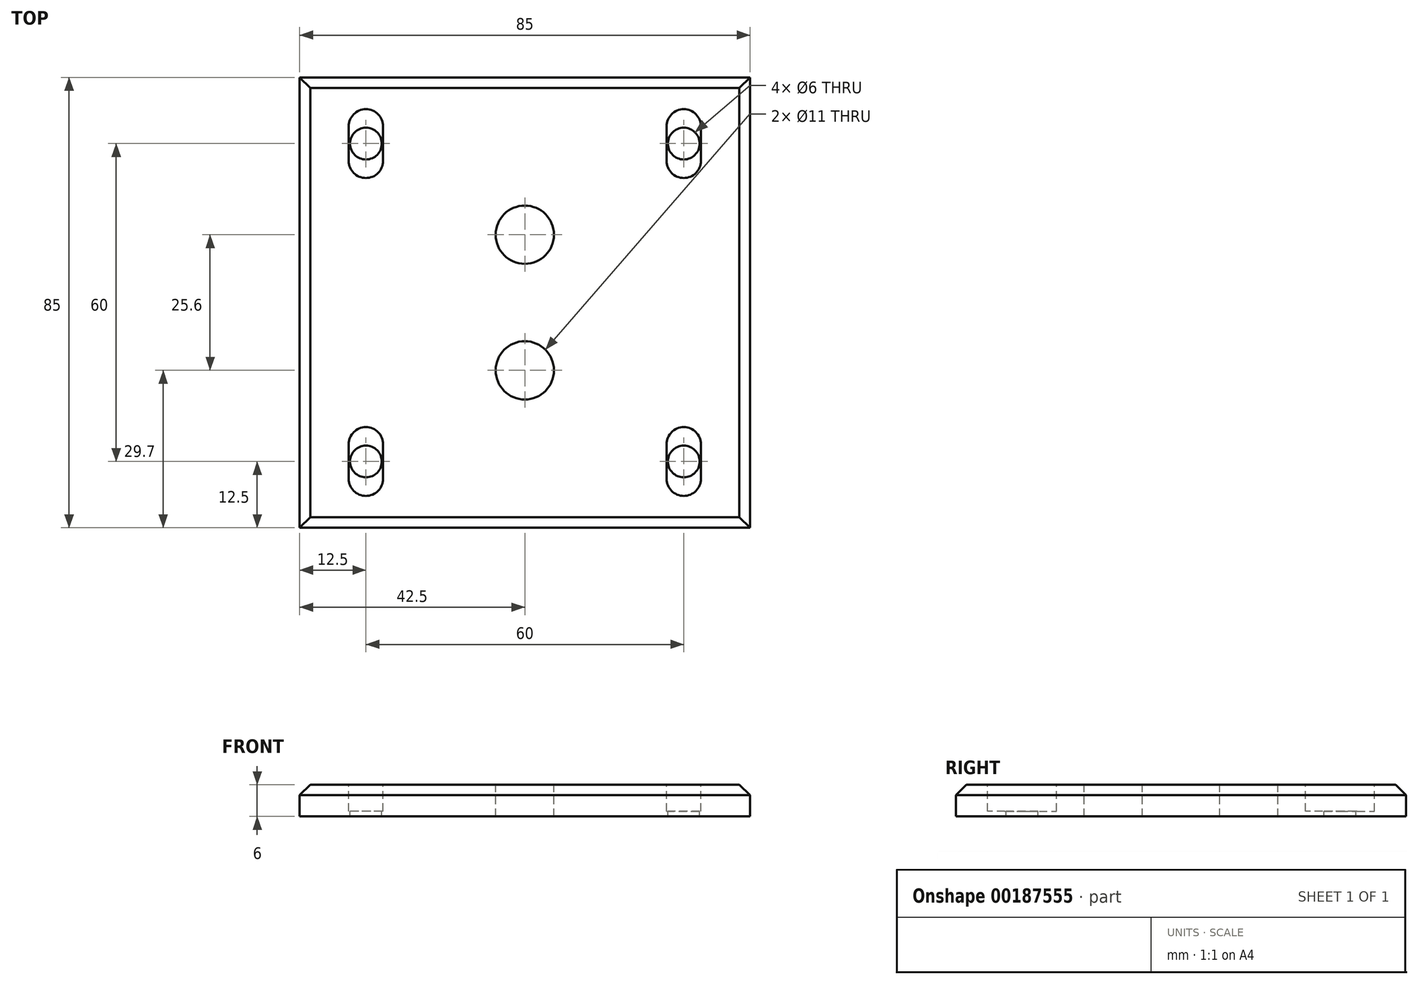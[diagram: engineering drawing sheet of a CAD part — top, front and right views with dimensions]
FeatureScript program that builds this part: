
annotation { "Feature Type Name" : "Feature", "Feature Type Description" : "" }
export const myFeature = defineFeature(function(context is Context, id is Id, definition is map)
    precondition{}
    {
        {
            var Q0;
            Q0=qCreatedBy(makeId("Top.planeOp"),FACE);
            var sketch = newSketch(context, id + "F0", { "sketchPlane" : qUnion([Q0])});
            skLineSegment(sketch, "E0.bottom", {"start": v(42.5, 42.5) * mm, "end": v(-42.5, 42.5) * mm});
            skLineSegment(sketch, "E0.top", {"start": v(42.5, -42.5) * mm, "end": v(-42.5, -42.5) * mm});
            skLineSegment(sketch, "E0.left", {"start": v(42.5, 42.5) * mm, "end": v(42.5, -42.5) * mm});
            skLineSegment(sketch, "E0.right", {"start": v(-42.5, 42.5) * mm, "end": v(-42.5, -42.5) * mm});
            skPoint(sketch, "E0.middle", {"position": v(0, 0) * mm});
            skSolve(sketch);
        }
        {
            var Q0;
            Q0=makeQuery(id+"F0.imprint","IMPRINT",FACE,{"disambiguationData":[TD([[makeQuery(id+"F0.imprint","IMPRINT",EDGE,{"derivedFrom":sQuery(id+"F0.wireOp",EDGE,"E0.bottom")}),1.0]])]});
            extrude(context, id + "F1", {"entities" : qUnion([Q0]), "depth" : 6 * mm});
        }
        {
            var Q0;
            Q0=makeQuery(id+"F1.opExtrude","CAP_FACE",FACE,{"disambiguationData":[OSD([sQuery(id+"F0.wireOp",EDGE,"E0.bottom"),sQuery(id+"F0.wireOp",EDGE,"E0.top"),sQuery(id+"F0.wireOp",EDGE,"E0.left"),sQuery(id+"F0.wireOp",EDGE,"E0.right")])],"isStart":false});
            var sketch = newSketch(context, id + "F2", { "sketchPlane" : qUnion([Q0])});
            skLineSegment(sketch, "E1", {"start": v(0, 42.5) * mm, "end": v(0, -42.5) * mm, "construction": true});
            skCircle(sketch, "E2", {"center": v(0, 12.8) * mm, "radius": 5.5 * mm});
            skCircle(sketch, "E3.MirrorC", {"center": v(0, -12.8) * mm, "radius": 5.5 * mm});
            skSolve(sketch);
        }
        {
            var Q0;
            Q0=qSketchRegion(id+"F2",true);
            extrude(context, id + "F3", {"entities" : qUnion([Q0]), "operationType" : NewBodyOperationType.REMOVE, "endBound" : BoundingType.THROUGH_ALL, "oppositeDirection" : true, "depth" : 25 * mm});
        }
        {
            var Q0;
            Q0=makeQuery(id+"F1.opExtrude","CAP_FACE",FACE,{"disambiguationData":[OSD([sQuery(id+"F0.wireOp",EDGE,"E0.bottom"),sQuery(id+"F0.wireOp",EDGE,"E0.top"),sQuery(id+"F0.wireOp",EDGE,"E0.left"),sQuery(id+"F0.wireOp",EDGE,"E0.right")])],"isStart":false});
            var sketch = newSketch(context, id + "F4", { "sketchPlane" : qUnion([Q0])});
            skLineSegment(sketch, "E4", {"start": v(-42.5, 0) * mm, "end": v(42.5, 0) * mm, "construction": true});
            skLineSegment(sketch, "E5.bottom", {"start": v(30, 30) * mm, "end": v(-30, 30) * mm, "construction": true});
            skLineSegment(sketch, "E5.top", {"start": v(30, -30) * mm, "end": v(-30, -30) * mm, "construction": true});
            skLineSegment(sketch, "E5.left", {"start": v(30, 30) * mm, "end": v(30, -30) * mm, "construction": true});
            skLineSegment(sketch, "E5.right", {"start": v(-30, 30) * mm, "end": v(-30, -30) * mm, "construction": true});
            skPoint(sketch, "E5.middle", {"position": v(0, 0) * mm});
            skCircle(sketch, "E6", {"center": v(-30, 30) * mm, "radius": 8.25 * mm, "construction": true});
            skCircle(sketch, "E7", {"center": v(30, 30) * mm, "radius": 8.25 * mm, "construction": true});
            skCircle(sketch, "E8", {"center": v(30, -30) * mm, "radius": 8.25 * mm, "construction": true});
            skCircle(sketch, "E9", {"center": v(-30, -30) * mm, "radius": 8.25 * mm, "construction": true});
            skCircle(sketch, "E10", {"center": v(30, 30) * mm, "radius": 8 * mm});
            skCircle(sketch, "E11", {"center": v(30, -30) * mm, "radius": 8 * mm});
            skCircle(sketch, "E12", {"center": v(-30, -30) * mm, "radius": 8 * mm});
            skCircle(sketch, "E13", {"center": v(-30, 30) * mm, "radius": 8 * mm});
            skSolve(sketch);
        }
        {
            var Q0;
            Q0=sQuery(id+"F4.wireOp",VERTEX,"E5.right.end");
            var Q1;
            Q1=sQuery(id+"F4.wireOp",VERTEX,"E13.center");
            var Q2;
            Q2=sQuery(id+"F4.wireOp",VERTEX,"E7.center");
            var Q3;
            Q3=sQuery(id+"F4.wireOp",VERTEX,"E5.left.end");
            var Q4;
            Q4=makeQuery(id+"F1.opExtrude","SWEPT_BODY",BODY,{"disambiguationData":[OSD([sQuery(id+"F0.wireOp",EDGE,"E0.bottom"),sQuery(id+"F0.wireOp",EDGE,"E0.top"),sQuery(id+"F0.wireOp",EDGE,"E0.left"),sQuery(id+"F0.wireOp",EDGE,"E0.right")])]});
            hole(context, id + "F5", {"style" : HoleStyle.SIMPLE, "endStyle" : HoleEndStyle.THROUGH, "holeDiameter" : 6 * mm, "locations" : qUnion([Q0, Q1, Q2, Q3]), "scope" : qUnion([Q4]), "isTappedThrough" : true});
        }
        {
            var Q0;
            Q0=makeQuery(id+"F1.opExtrude","CAP_EDGE",EDGE,{"disambiguationData":[OSD([sQuery(id+"F0.wireOp",EDGE,"E0.right")])],"isStart":false});
            var Q1;
            Q1=makeQuery(id+"F1.opExtrude","CAP_EDGE",EDGE,{"disambiguationData":[OSD([sQuery(id+"F0.wireOp",EDGE,"E0.top")])],"isStart":false});
            var Q2;
            Q2=makeQuery(id+"F1.opExtrude","CAP_EDGE",EDGE,{"disambiguationData":[OSD([sQuery(id+"F0.wireOp",EDGE,"E0.left")])],"isStart":false});
            var Q3;
            Q3=makeQuery(id+"F1.opExtrude","CAP_EDGE",EDGE,{"disambiguationData":[OSD([sQuery(id+"F0.wireOp",EDGE,"E0.bottom")])],"isStart":false});
            chamfer(context, id + "F6", {"entities" : qUnion([Q0, Q1, Q2, Q3]), "width" : 2 * mm, "tangentPropagation" : true});
        }
        {
            var Q0;
            Q0=makeQuery(id+"F4.imprint","IMPRINT",FACE,{"disambiguationData":[TD([[makeQuery(id+"F4.imprint","IMPRINT",EDGE,{"derivedFrom":sQuery(id+"F4.wireOp",EDGE,"E10")}),-1.0]])]});
            var sketch = newSketch(context, id + "F7", { "sketchPlane" : qUnion([Q0])});
            skPoint(sketch, "E14.0", {"position": v(30, 30) * mm});
            skPoint(sketch, "E15.0", {"position": v(-30, 30) * mm});
            skPoint(sketch, "E16.0", {"position": v(30, -30) * mm});
            skPoint(sketch, "E17.0", {"position": v(-30, -30) * mm});
            skCircle(sketch, "E18", {"center": v(30, 30) * mm, "radius": 3.25 * mm, "construction": true});
            skLineSegment(sketch, "E19.0", {"start": v(30, 33.25) * mm, "end": v(30, 26.75) * mm, "construction": true});
            skLineSegment(sketch, "E20.0", {"start": v(-30, 30) * mm, "end": v(-30, -30) * mm, "construction": true});
            skLineSegment(sketch, "E21.0", {"start": v(30, -30) * mm, "end": v(-30, -30) * mm, "construction": true});
            skArc(sketch, "E22.0.startCap", {"start": v(26.75, 33.25) * mm, "mid": v(30, 36.5) * mm, "end": v(33.25, 33.25) * mm});
            skArc(sketch, "E22.0.endCap", {"start": v(33.25, 26.75) * mm, "mid": v(30, 23.5) * mm, "end": v(26.75, 26.75) * mm});
            skLineSegment(sketch, "E22.0.left", {"start": v(33.25, 33.25) * mm, "end": v(33.25, 26.75) * mm});
            skLineSegment(sketch, "E22.0.right", {"start": v(26.75, 33.25) * mm, "end": v(26.75, 26.75) * mm});
            skCircle(sketch, "E23.MirrorC", {"center": v(-30, 30) * mm, "radius": 3.25 * mm, "construction": true});
            skArc(sketch, "E24.MirrorCS", {"start": v(-26.75, 33.25) * mm, "mid": v(-30, 36.5) * mm, "end": v(-33.25, 33.25) * mm});
            skArc(sketch, "E25.MirrorCS", {"start": v(-33.25, 26.75) * mm, "mid": v(-30, 23.5) * mm, "end": v(-26.75, 26.75) * mm});
            skLineSegment(sketch, "E26.MirrorCS", {"start": v(-33.25, 33.25) * mm, "end": v(-33.25, 26.75) * mm});
            skLineSegment(sketch, "E27.MirrorCS", {"start": v(-30, 33.25) * mm, "end": v(-30, 26.75) * mm, "construction": true});
            skLineSegment(sketch, "E28.MirrorCS", {"start": v(-26.75, 33.25) * mm, "end": v(-26.75, 26.75) * mm});
            skLineSegment(sketch, "E29.MirrorCS", {"start": v(-30, -33.25) * mm, "end": v(-30, -26.75) * mm, "construction": true});
            skLineSegment(sketch, "E30.MirrorCS", {"start": v(30, -33.25) * mm, "end": v(30, -26.75) * mm, "construction": true});
            skArc(sketch, "E31.MirrorCS", {"start": v(26.75, -33.25) * mm, "mid": v(30, -36.5) * mm, "end": v(33.25, -33.25) * mm});
            skLineSegment(sketch, "E32.MirrorCS", {"start": v(-26.75, -33.25) * mm, "end": v(-26.75, -26.75) * mm});
            skArc(sketch, "E33.MirrorCS", {"start": v(-33.25, -26.75) * mm, "mid": v(-30, -23.5) * mm, "end": v(-26.75, -26.75) * mm});
            skLineSegment(sketch, "E34.MirrorCS", {"start": v(-33.25, -33.25) * mm, "end": v(-33.25, -26.75) * mm});
            skCircle(sketch, "E35.MirrorC", {"center": v(-30, -30) * mm, "radius": 3.25 * mm, "construction": true});
            skArc(sketch, "E36.MirrorCS", {"start": v(-26.75, -33.25) * mm, "mid": v(-30, -36.5) * mm, "end": v(-33.25, -33.25) * mm});
            skCircle(sketch, "E37.MirrorC", {"center": v(30, -30) * mm, "radius": 3.25 * mm, "construction": true});
            skLineSegment(sketch, "E38.MirrorCS", {"start": v(26.75, -33.25) * mm, "end": v(26.75, -26.75) * mm});
            skLineSegment(sketch, "E39.MirrorCS", {"start": v(33.25, -33.25) * mm, "end": v(33.25, -26.75) * mm});
            skArc(sketch, "E40.MirrorCS", {"start": v(33.25, -26.75) * mm, "mid": v(30, -23.5) * mm, "end": v(26.75, -26.75) * mm});
            skSolve(sketch);
        }
        {
            var Q0;
            Q0 = qSketchRegion(id + "F7", true);
            extrude(context, id + "F8", {"entities" : qUnion([Q0]), "operationType" : NewBodyOperationType.REMOVE, "oppositeDirection" : true, "depth" : 5 * mm});
        }
    });
